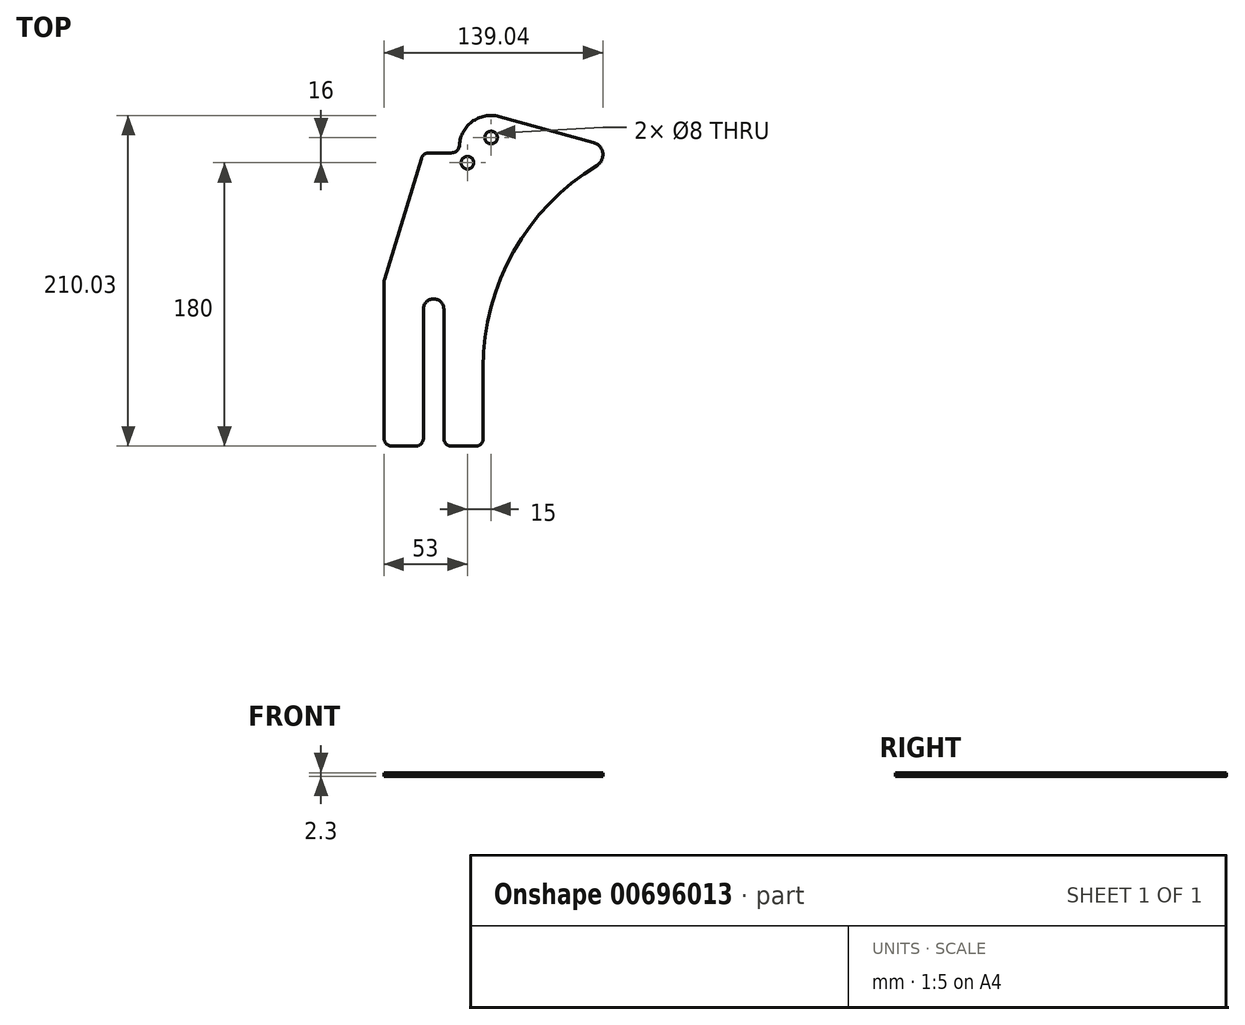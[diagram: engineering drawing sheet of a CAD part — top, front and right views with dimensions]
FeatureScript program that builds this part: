
annotation { "Feature Type Name" : "Feature", "Feature Type Description" : "" }
export const myFeature = defineFeature(function(context is Context, id is Id, definition is map)
    precondition{}
    {
        {
            var Q0;
            Q0=qCreatedBy(makeId("Top.planeOp"),FACE);
            var sketch = newSketch(context, id + "F0", { "sketchPlane" : qUnion([Q0])});
            skLineSegment(sketch, "E0", {"start": v(0, 5) * mm, "end": v(0, 104.25) * mm});
            skLineSegment(sketch, "E1", {"start": v(0.22, 105.71) * mm, "end": v(23.77, 182.75) * mm});
            skLineSegment(sketch, "E2", {"start": v(28.55, 186.29) * mm, "end": v(42.85, 186.29) * mm});
            skLineSegment(sketch, "E3", {"start": v(47.85, 190.03) * mm, "end": v(47.85, 191.29) * mm});
            skLineSegment(sketch, "E4", {"start": v(73.16, 209.32) * mm, "end": v(133.16, 192.8) * mm});
            skLineSegment(sketch, "E5", {"start": v(5, 0) * mm, "end": v(20, 0) * mm});
            skLineSegment(sketch, "E6", {"start": v(25, 5) * mm, "end": v(25, 87) * mm});
            skLineSegment(sketch, "E7", {"start": v(31.5, 87) * mm, "end": v(38, 87) * mm, "construction": true});
            skLineSegment(sketch, "E8", {"start": v(38, 87) * mm, "end": v(38, 5) * mm});
            skLineSegment(sketch, "E9", {"start": v(43, 0) * mm, "end": v(58, 0) * mm});
            skLineSegment(sketch, "E10", {"start": v(63, 5) * mm, "end": v(63, 50) * mm});
            skLineSegment(sketch, "E11", {"start": v(24.85, 186.29) * mm, "end": v(47.85, 186.29) * mm, "construction": true});
            skLineSegment(sketch, "E12", {"start": v(233.9, 186.29) * mm, "end": v(47.85, 186.29) * mm, "construction": true});
            skPoint(sketch, "E13", {"position": v(213, 50) * mm});
            skArc(sketch, "E14", {"start": v(135.2, 178.24) * mm, "mid": v(82.29, 123.58) * mm, "end": v(63, 50) * mm});
            skArc(sketch, "E15", {"start": v(38, 87) * mm, "mid": v(31.5, 93.5) * mm, "end": v(25, 87) * mm});
            skPoint(sketch, "E16.start.orphan", {"position": v(63, 67.37) * mm});
            skPoint(sketch, "E17", {"position": v(152.8, 187.39) * mm});
            skPoint(sketch, "E18.orphan", {"position": v(156.8, 186.29) * mm});
            skPoint(sketch, "E19.visualSharp", {"position": v(63, 0) * mm});
            skArc(sketch, "E19.filletArc", {"start": v(58, 0) * mm, "mid": v(61.54, 1.46) * mm, "end": v(63, 5) * mm});
            skPoint(sketch, "E20.visualSharp", {"position": v(38, 0) * mm});
            skArc(sketch, "E20.filletArc", {"start": v(38, 5) * mm, "mid": v(39.46, 1.46) * mm, "end": v(43, 0) * mm});
            skPoint(sketch, "E21.visualSharp", {"position": v(25, 0) * mm});
            skArc(sketch, "E21.filletArc", {"start": v(20, 0) * mm, "mid": v(23.54, 1.46) * mm, "end": v(25, 5) * mm});
            skPoint(sketch, "E22.visualSharp", {"position": v(0, 0) * mm});
            skArc(sketch, "E22.filletArc", {"start": v(0, 5) * mm, "mid": v(1.46, 1.46) * mm, "end": v(5, 0) * mm});
            skPoint(sketch, "E23.visualSharp", {"position": v(0, 105) * mm});
            skArc(sketch, "E23.filletArc", {"start": v(0.22, 105.71) * mm, "mid": v(0.05, 105) * mm, "end": v(0, 104.25) * mm});
            skPoint(sketch, "E24.visualSharp", {"position": v(24.85, 186.29) * mm});
            skArc(sketch, "E24.filletArc", {"start": v(28.55, 186.29) * mm, "mid": v(25.58, 185.3) * mm, "end": v(23.77, 182.75) * mm});
            skPoint(sketch, "E25.visualSharp", {"position": v(47.85, 186.29) * mm});
            skArc(sketch, "E25.filletArc", {"start": v(42.85, 186.29) * mm, "mid": v(46.39, 187.75) * mm, "end": v(47.85, 191.29) * mm});
            skPoint(sketch, "E26.visualSharp", {"position": v(47.85, 216.29) * mm});
            skArc(sketch, "E26.filletArc", {"start": v(73.16, 209.32) * mm, "mid": v(55.73, 205.94) * mm, "end": v(47.85, 190.03) * mm});
            skArc(sketch, "E27.filletArc", {"start": v(135.2, 178.24) * mm, "mid": v(138.96, 186.18) * mm, "end": v(133.16, 192.8) * mm});
            skPoint(sketch, "E28", {"position": v(53, 180) * mm});
            skCircle(sketch, "E29", {"center": v(53, 180) * mm, "radius": 4 * mm});
            skPoint(sketch, "E30", {"position": v(68, 196) * mm});
            skCircle(sketch, "E31", {"center": v(68, 196) * mm, "radius": 4 * mm});
            skSolve(sketch);
        }
        {
            var Q0;
            Q0=makeQuery(id+"F0.imprint","IMPRINT",FACE,{"disambiguationData":[TD([[makeQuery(id+"F0.imprint","IMPRINT",EDGE,{"derivedFrom":sQuery(id+"F0.wireOp",EDGE,"E0")}),-1.0]])]});
            extrude(context, id + "F1", {"entities" : qUnion([Q0]), "endBound" : BoundingType.SYMMETRIC, "depth" : 2.3 * mm, "offsetDistance" : 25 * mm});
        }
        {
            var Q0;
            Q0=makeQuery(id+"F1.opExtrude","CAP_VERTEX",VERTEX,{"disambiguationData":[OSD([sQuery(id+"F0.wireOp",EDGE,"E10"),sQuery(id+"F0.wireOp",EDGE,"E14")])],"isStart":false});
            var Q1;
            Q1=qCreatedBy(makeId("Front.planeOp"),FACE);
            cPlane(context, id + "F2", {"entities" : qUnion([Q0, Q1]), "cplaneType" : CPlaneType.PLANE_POINT, "offset" : 25 * mm, "width" : 150 * mm, "height" : 150 * mm});
        }
    });
